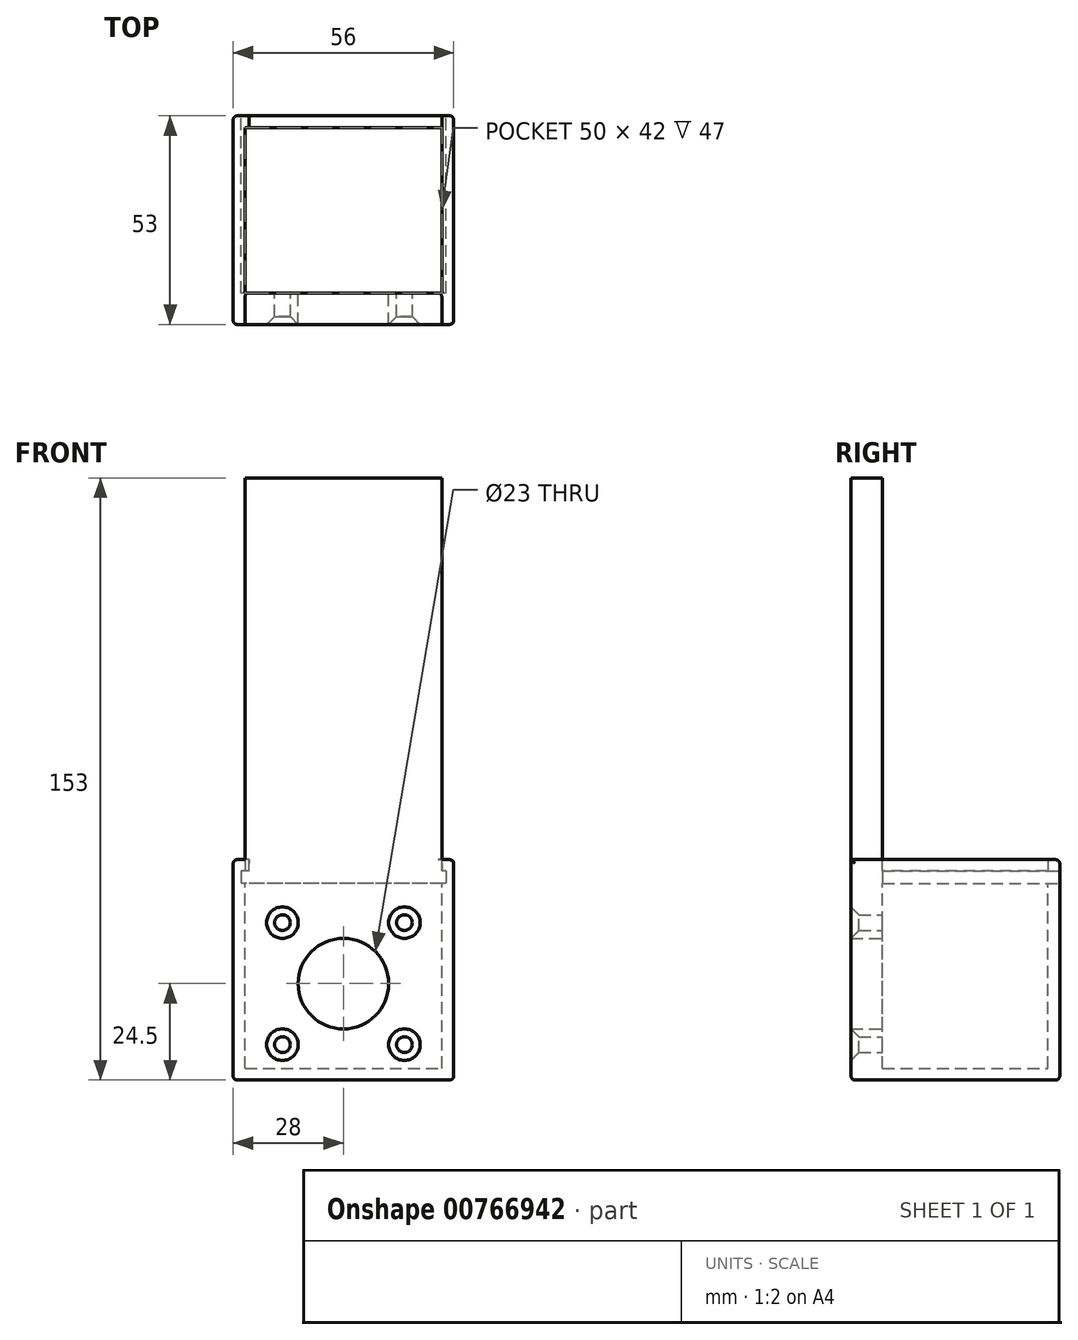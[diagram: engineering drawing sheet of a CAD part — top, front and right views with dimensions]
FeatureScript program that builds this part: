
annotation { "Feature Type Name" : "Feature", "Feature Type Description" : "" }
export const myFeature = defineFeature(function(context is Context, id is Id, definition is map)
    precondition{}
    {
        {
            var Q0;
            Q0=qCreatedBy(makeId("Front.planeOp"),FACE);
            var sketch = newSketch(context, id + "F0", { "sketchPlane" : qUnion([Q0])});
            skLineSegment(sketch, "E0.bottom", {"start": v(0, 0) * mm, "end": v(50, 0) * mm});
            skLineSegment(sketch, "E0.top", {"start": v(0, 150) * mm, "end": v(50, 150) * mm});
            skLineSegment(sketch, "E0.left", {"start": v(0, 0) * mm, "end": v(0, 150) * mm});
            skLineSegment(sketch, "E0.right", {"start": v(50, 0) * mm, "end": v(50, 150) * mm});
            skCircle(sketch, "E1", {"center": v(25, 21.5) * mm, "radius": 11.5 * mm});
            skCircle(sketch, "E2", {"center": v(9.5, 37) * mm, "radius": 2 * mm});
            skCircle(sketch, "E3", {"center": v(9.5, 6) * mm, "radius": 2 * mm});
            skCircle(sketch, "E4", {"center": v(40.5, 6) * mm, "radius": 2 * mm});
            skCircle(sketch, "E5", {"center": v(40.5, 37) * mm, "radius": 2 * mm});
            skSolve(sketch);
        }
        {
            var Q0;
            Q0 = qSketchRegion(id + "F0", true);
            extrude(context, id + "F1", {"entities" : qUnion([Q0]), "depth" : 8 * mm, "offsetDistance" : 25 * mm});
        }
        {
            var Q0;
            Q0=makeQuery(id+"F1.opExtrude","CAP_EDGE",EDGE,{"disambiguationData":[OSD([sQuery(id+"F0.wireOp",EDGE,"E2")])],"isStart":false});
            var Q1;
            Q1=makeQuery(id+"F1.opExtrude","CAP_EDGE",EDGE,{"disambiguationData":[OSD([sQuery(id+"F0.wireOp",EDGE,"E5")])],"isStart":false});
            var Q2;
            Q2=makeQuery(id+"F1.opExtrude","CAP_EDGE",EDGE,{"disambiguationData":[OSD([sQuery(id+"F0.wireOp",EDGE,"E4")])],"isStart":false});
            var Q3;
            Q3=makeQuery(id+"F1.opExtrude","CAP_EDGE",EDGE,{"disambiguationData":[OSD([sQuery(id+"F0.wireOp",EDGE,"E3")])],"isStart":false});
            chamfer(context, id + "F2", {"entities" : qUnion([Q0, Q1, Q2, Q3]), "width" : 2 * mm, "tangentPropagation" : true});
        }
        {
            var Q0;
            Q0=makeQuery(id+"F1.opExtrude","SWEPT_FACE",FACE,{"disambiguationData":[OSD([sQuery(id+"F0.wireOp",EDGE,"E0.right")])]});
            var sketch = newSketch(context, id + "F3", { "sketchPlane" : qUnion([Q0])});
            skLineSegment(sketch, "E6.bottom", {"start": v(-8, 0) * mm, "end": v(42, 0) * mm});
            skLineSegment(sketch, "E6.top", {"start": v(-8, 53) * mm, "end": v(42, 53) * mm});
            skLineSegment(sketch, "E6.left", {"start": v(-8, 0) * mm, "end": v(-8, 53) * mm});
            skLineSegment(sketch, "E6.right", {"start": v(42, 0) * mm, "end": v(42, 53) * mm});
            skSolve(sketch);
        }
        {
            var Q0;
            Q0 = qSketchRegion(id + "F3", true);
            extrude(context, id + "F4", {"entities" : qUnion([Q0]), "operationType" : NewBodyOperationType.ADD, "depth" : 3 * mm, "offsetDistance" : 25 * mm});
        }
        {
            var Q0;
            Q0=makeQuery(id+"F1.opExtrude","SWEPT_FACE",FACE,{"disambiguationData":[OSD([sQuery(id+"F0.wireOp",EDGE,"E0.left")])]});
            var sketch = newSketch(context, id + "F5", { "sketchPlane" : qUnion([Q0])});
            skLineSegment(sketch, "E7.bottom", {"start": v(8, 53) * mm, "end": v(-42, 53) * mm});
            skLineSegment(sketch, "E7.top", {"start": v(8, 0) * mm, "end": v(-42, 0) * mm});
            skLineSegment(sketch, "E7.left", {"start": v(8, 53) * mm, "end": v(8, 0) * mm});
            skLineSegment(sketch, "E7.right", {"start": v(-42, 53) * mm, "end": v(-42, 0) * mm});
            skSolve(sketch);
        }
        {
            var Q0;
            Q0 = qSketchRegion(id + "F5", true);
            extrude(context, id + "F6", {"entities" : qUnion([Q0]), "operationType" : NewBodyOperationType.ADD, "depth" : 3 * mm, "offsetDistance" : 25 * mm});
        }
        {
            var Q0;
            Q0=makeQuery(id+"F6.boolean.opBoolean","MERGE",FACE,{"derivedFrom":[makeQuery(id+"F4.boolean.opBoolean","MERGE",FACE,{"derivedFrom":[makeQuery(id+"F1.opExtrude","SWEPT_FACE",FACE,{"disambiguationData":[OSD([sQuery(id+"F0.wireOp",EDGE,"E0.bottom")])]}),makeQuery(id+"F4.opExtrude","SWEPT_FACE",FACE,{"disambiguationData":[OSD([sQuery(id+"F3.wireOp",EDGE,"E6.bottom")])]})]}),makeQuery(id+"F6.opExtrude","SWEPT_FACE",FACE,{"disambiguationData":[OSD([sQuery(id+"F5.wireOp",EDGE,"E7.top")])]})]});
            var sketch = newSketch(context, id + "F7", { "sketchPlane" : qUnion([Q0])});
            skLineSegment(sketch, "E8.bottom", {"start": v(-3, 8) * mm, "end": v(53, 8) * mm});
            skLineSegment(sketch, "E8.top", {"start": v(-3, -42) * mm, "end": v(53, -42) * mm});
            skLineSegment(sketch, "E8.left", {"start": v(-3, 8) * mm, "end": v(-3, -42) * mm});
            skLineSegment(sketch, "E8.right", {"start": v(53, 8) * mm, "end": v(53, -42) * mm});
            skSolve(sketch);
        }
        {
            var Q0;
            Q0 = qSketchRegion(id + "F7", true);
            extrude(context, id + "F8", {"entities" : qUnion([Q0]), "operationType" : NewBodyOperationType.ADD, "depth" : 3 * mm, "offsetDistance" : 25 * mm});
        }
        {
            var Q0;
            Q0=makeQuery(id+"F8.boolean.opBoolean","MERGE",FACE,{"derivedFrom":[makeQuery(id+"F4.opExtrude","SWEPT_FACE",FACE,{"disambiguationData":[OSD([sQuery(id+"F3.wireOp",EDGE,"E6.right")])]}),makeQuery(id+"F6.opExtrude","SWEPT_FACE",FACE,{"disambiguationData":[OSD([sQuery(id+"F5.wireOp",EDGE,"E7.right")])]}),makeQuery(id+"F8.opExtrude","SWEPT_FACE",FACE,{"disambiguationData":[OSD([sQuery(id+"F7.wireOp",EDGE,"E8.top")])]})]});
            var sketch = newSketch(context, id + "F9", { "sketchPlane" : qUnion([Q0])});
            skLineSegment(sketch, "E9.bottom", {"start": v(-53, 53) * mm, "end": v(3, 53) * mm});
            skLineSegment(sketch, "E9.top", {"start": v(-53, -3) * mm, "end": v(3, -3) * mm});
            skLineSegment(sketch, "E9.left", {"start": v(-53, 53) * mm, "end": v(-53, -3) * mm});
            skLineSegment(sketch, "E9.right", {"start": v(3, 53) * mm, "end": v(3, -3) * mm});
            skSolve(sketch);
        }
        {
            var Q0;
            Q0 = qSketchRegion(id + "F9", true);
            extrude(context, id + "F10", {"entities" : qUnion([Q0]), "operationType" : NewBodyOperationType.ADD, "depth" : 3 * mm, "offsetDistance" : 25 * mm});
        }
        {
            var Q0;
            {var subQ0=sQuery(id+"F0.wireOp",EDGE,"E0.right");Q0=makeQuery(id+"F4.boolean.opBoolean","SPLIT",EDGE,{"disambiguationData":[topologyDisambiguationEdgeConnected([makeQuery(id+"F4.opExtrude","CAP_FACE",FACE,{"disambiguationData":[OSD([sQuery(id+"F3.wireOp",EDGE,"E6.bottom"),sQuery(id+"F3.wireOp",EDGE,"E6.top"),sQuery(id+"F3.wireOp",EDGE,"E6.left"),sQuery(id+"F3.wireOp",EDGE,"E6.right")])],"isStart":true})])],"derivedFrom":makeQuery(id+"F1.opExtrude","CAP_EDGE",EDGE,{"disambiguationData":[OSD([subQ0])],"isStart":true})});}
            var Q1;
            Q1=makeQuery(id+"F1.opExtrude","CAP_EDGE",EDGE,{"disambiguationData":[OSD([sQuery(id+"F0.wireOp",EDGE,"E0.bottom")])],"isStart":true});
            var Q2;
            Q2=makeQuery(id+"F4.opExtrude","CAP_EDGE",EDGE,{"disambiguationData":[OSD([sQuery(id+"F3.wireOp",EDGE,"E6.bottom")])],"isStart":true});
            var Q3;
            Q3=makeQuery(id+"F6.opExtrude","CAP_EDGE",EDGE,{"disambiguationData":[OSD([sQuery(id+"F5.wireOp",EDGE,"E7.top")])],"isStart":true});
            var Q4;
            Q4=makeQuery(id+"F6.opExtrude","CAP_EDGE",EDGE,{"disambiguationData":[OSD([sQuery(id+"F5.wireOp",EDGE,"E7.right")])],"isStart":true});
            var Q5;
            Q5=makeQuery(id+"F4.opExtrude","CAP_EDGE",EDGE,{"disambiguationData":[OSD([sQuery(id+"F3.wireOp",EDGE,"E6.right")])],"isStart":true});
            var Q6;
            {var subQ0=sQuery(id+"F0.wireOp",EDGE,"E0.left");Q6=makeQuery(id+"F6.boolean.opBoolean","SPLIT",EDGE,{"disambiguationData":[topologyDisambiguationEdgeConnected([makeQuery(id+"F6.opExtrude","CAP_FACE",FACE,{"disambiguationData":[OSD([sQuery(id+"F5.wireOp",EDGE,"E7.bottom"),sQuery(id+"F5.wireOp",EDGE,"E7.top"),sQuery(id+"F5.wireOp",EDGE,"E7.left"),sQuery(id+"F5.wireOp",EDGE,"E7.right")])],"isStart":true})])],"derivedFrom":makeQuery(id+"F1.opExtrude","CAP_EDGE",EDGE,{"disambiguationData":[OSD([subQ0])],"isStart":true})});}
            var Q7;
            Q7=makeQuery(id+"F8.opExtrude","CAP_EDGE",EDGE,{"disambiguationData":[OSD([sQuery(id+"F7.wireOp",EDGE,"E8.top")])],"isStart":true});
            var Q8;
            Q8=makeQuery(id+"F10.opExtrude","CAP_EDGE",EDGE,{"disambiguationData":[OSD([sQuery(id+"F9.wireOp",EDGE,"E9.left")])],"isStart":false});
            var Q9;
            Q9=makeQuery(id+"F10.opExtrude","CAP_FACE",FACE,{"disambiguationData":[OSD([sQuery(id+"F9.wireOp",EDGE,"E9.bottom"),sQuery(id+"F9.wireOp",EDGE,"E9.top"),sQuery(id+"F9.wireOp",EDGE,"E9.left"),sQuery(id+"F9.wireOp",EDGE,"E9.right")])],"isStart":false});
            var Q10;
            Q10=makeQuery(id+"F10.boolean.opBoolean","MERGE",FACE,{"derivedFrom":[makeQuery(id+"F8.opExtrude","CAP_FACE",FACE,{"disambiguationData":[OSD([sQuery(id+"F7.wireOp",EDGE,"E8.bottom"),sQuery(id+"F7.wireOp",EDGE,"E8.top"),sQuery(id+"F7.wireOp",EDGE,"E8.left"),sQuery(id+"F7.wireOp",EDGE,"E8.right")])],"isStart":false}),makeQuery(id+"F10.opExtrude","SWEPT_FACE",FACE,{"disambiguationData":[OSD([sQuery(id+"F9.wireOp",EDGE,"E9.top")])]})]});
            var Q11;
            Q11=makeQuery(id+"F10.boolean.opBoolean","MERGE",FACE,{"derivedFrom":[makeQuery(id+"F8.boolean.opBoolean","MERGE",FACE,{"derivedFrom":[makeQuery(id+"F4.opExtrude","CAP_FACE",FACE,{"disambiguationData":[OSD([sQuery(id+"F3.wireOp",EDGE,"E6.bottom"),sQuery(id+"F3.wireOp",EDGE,"E6.top"),sQuery(id+"F3.wireOp",EDGE,"E6.left"),sQuery(id+"F3.wireOp",EDGE,"E6.right")])],"isStart":false}),makeQuery(id+"F8.opExtrude","SWEPT_FACE",FACE,{"disambiguationData":[OSD([sQuery(id+"F7.wireOp",EDGE,"E8.right")])]})]}),makeQuery(id+"F10.opExtrude","SWEPT_FACE",FACE,{"disambiguationData":[OSD([sQuery(id+"F9.wireOp",EDGE,"E9.left")])]})]});
            var Q12;
            Q12=makeQuery(id+"F10.boolean.opBoolean","MERGE",FACE,{"derivedFrom":[makeQuery(id+"F8.boolean.opBoolean","MERGE",FACE,{"derivedFrom":[makeQuery(id+"F6.opExtrude","CAP_FACE",FACE,{"disambiguationData":[OSD([sQuery(id+"F5.wireOp",EDGE,"E7.bottom"),sQuery(id+"F5.wireOp",EDGE,"E7.top"),sQuery(id+"F5.wireOp",EDGE,"E7.left"),sQuery(id+"F5.wireOp",EDGE,"E7.right")])],"isStart":false}),makeQuery(id+"F8.opExtrude","SWEPT_FACE",FACE,{"disambiguationData":[OSD([sQuery(id+"F7.wireOp",EDGE,"E8.left")])]})]}),makeQuery(id+"F10.opExtrude","SWEPT_FACE",FACE,{"disambiguationData":[OSD([sQuery(id+"F9.wireOp",EDGE,"E9.right")])]})]});
            var Q13;
            Q13=makeQuery(id+"F10.opExtrude","CAP_EDGE",EDGE,{"disambiguationData":[OSD([sQuery(id+"F9.wireOp",EDGE,"E9.right")])],"isStart":false});
            fillet(context, id + "F11", {"entities" : qUnion([Q0, Q1, Q2, Q3, Q4, Q5, Q6, Q7, Q8, Q9, Q10, Q11, Q12, Q13]), "radius" : 1 * mm, "tangentPropagation" : true, "allowEdgeOverflow" : false});
        }
        {
            var Q0;
            Q0=makeQuery(id+"F10.opExtrude","CAP_FACE",FACE,{"disambiguationData":[OSD([sQuery(id+"F9.wireOp",EDGE,"E9.bottom"),sQuery(id+"F9.wireOp",EDGE,"E9.top"),sQuery(id+"F9.wireOp",EDGE,"E9.left"),sQuery(id+"F9.wireOp",EDGE,"E9.right")])],"isStart":false});
            var sketch = newSketch(context, id + "F12", { "sketchPlane" : qUnion([Q0])});
            skLineSegment(sketch, "E10.bottom", {"start": v(-51, 50.1) * mm, "end": v(-50, 50.1) * mm});
            skLineSegment(sketch, "E10.top", {"start": v(-51, 47) * mm, "end": v(1, 47) * mm});
            skLineSegment(sketch, "E10.left", {"start": v(-51, 50.1) * mm, "end": v(-51, 47) * mm});
            skLineSegment(sketch, "E10.right", {"start": v(1, 50.1) * mm, "end": v(1, 47) * mm});
            skLineSegment(sketch, "E11", {"start": v(-1, 50.1) * mm, "end": v(-1, 53) * mm});
            skLineSegment(sketch, "E12", {"start": v(-1, 53) * mm, "end": v(-50, 53) * mm});
            skLineSegment(sketch, "E13", {"start": v(-50, 53) * mm, "end": v(-50, 50.1) * mm});
            skLineSegment(sketch, "E14.trimOffspring", {"start": v(-1, 50.1) * mm, "end": v(1, 50.1) * mm});
            skSolve(sketch);
        }
        {
            var Q0;
            Q0 = qSketchRegion(id + "F12", true);
            var Q1;
            Q1=makeQuery(id+"F1.opExtrude","CAP_FACE",FACE,{"disambiguationData":[OSD([sQuery(id+"F0.wireOp",EDGE,"E0.bottom"),sQuery(id+"F0.wireOp",EDGE,"E0.top"),sQuery(id+"F0.wireOp",EDGE,"E0.left"),sQuery(id+"F0.wireOp",EDGE,"E0.right"),sQuery(id+"F0.wireOp",EDGE,"E1"),sQuery(id+"F0.wireOp",EDGE,"E2"),sQuery(id+"F0.wireOp",EDGE,"E3"),sQuery(id+"F0.wireOp",EDGE,"E4"),sQuery(id+"F0.wireOp",EDGE,"E5")])],"isStart":true});
            extrude(context, id + "F13", {"entities" : qUnion([Q0]), "operationType" : NewBodyOperationType.REMOVE, "endBound" : BoundingType.UP_TO_SURFACE, "oppositeDirection" : true, "depth" : 45 * mm, "endBoundEntityFace" : qUnion([Q1]), "offsetDistance" : 25 * mm});
        }
    });
